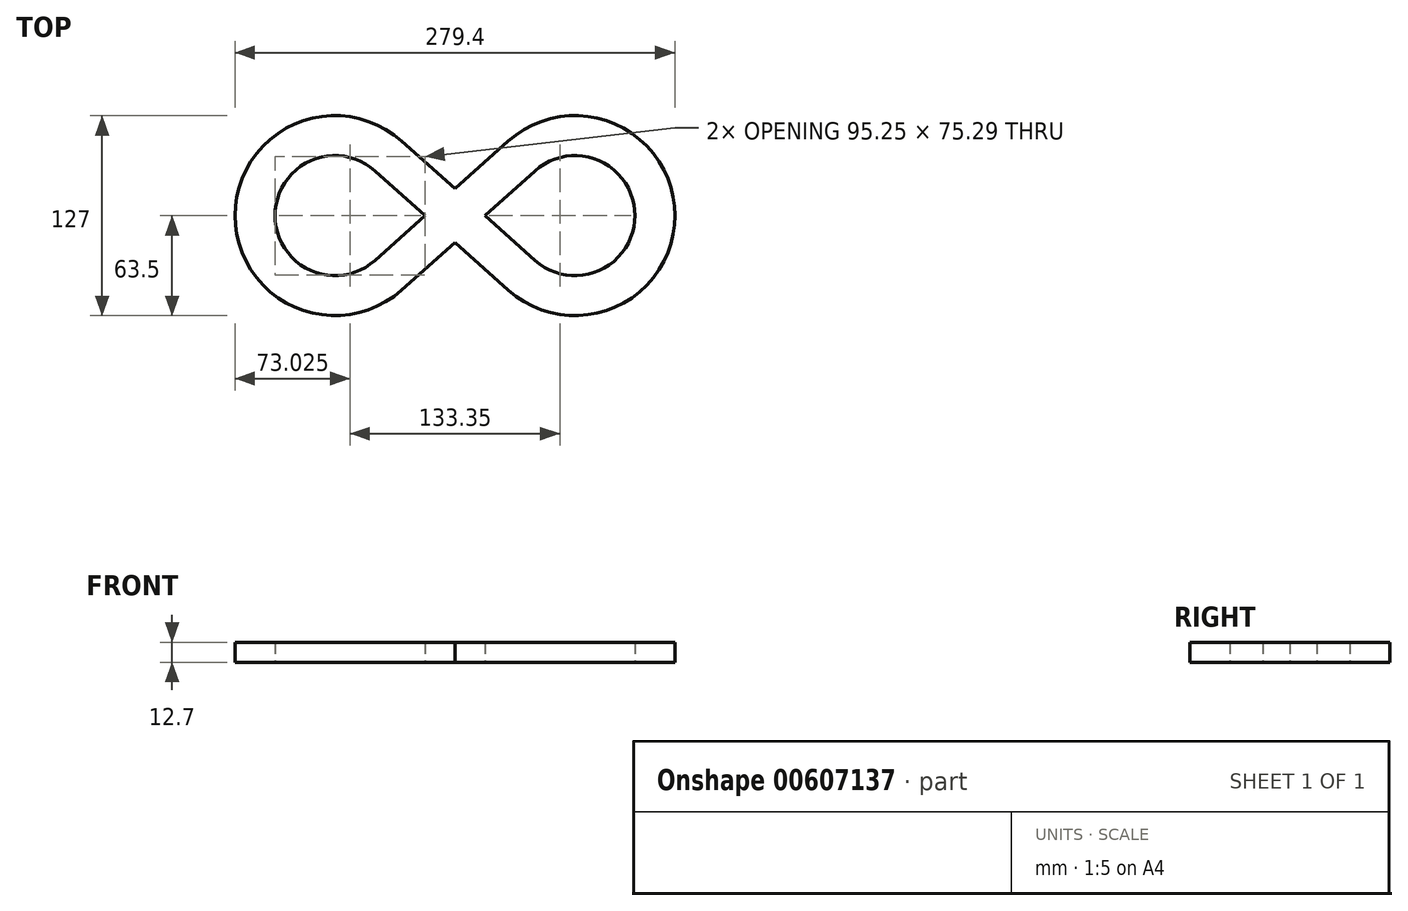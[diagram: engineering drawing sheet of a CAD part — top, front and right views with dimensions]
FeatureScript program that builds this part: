
annotation { "Feature Type Name" : "Feature", "Feature Type Description" : "" }
export const myFeature = defineFeature(function(context is Context, id is Id, definition is map)
    precondition{}
    {
        {
            var Q0;
            Q0=qCreatedBy(makeId("Top.planeOp"),FACE);
            var sketch = newSketch(context, id + "F0", { "sketchPlane" : qUnion([Q0])});
            skArc(sketch, "E0", {"start": v(-50.8, 28.4) * mm, "mid": v(-114.3, 0) * mm, "end": v(-50.8, -28.4) * mm});
            skArc(sketch, "E1", {"start": v(-33.87, 47.33) * mm, "mid": v(-139.7, 0) * mm, "end": v(-33.87, -47.33) * mm});
            skArc(sketch, "E2", {"start": v(33.87, -47.33) * mm, "mid": v(139.7, 0) * mm, "end": v(33.87, 47.33) * mm});
            skArc(sketch, "E3", {"start": v(50.8, -28.4) * mm, "mid": v(114.3, 0) * mm, "end": v(50.8, 28.4) * mm});
            skLineSegment(sketch, "E4", {"start": v(-33.87, 47.33) * mm, "end": v(50.8, -28.4) * mm});
            skLineSegment(sketch, "E5", {"start": v(-50.8, 28.4) * mm, "end": v(33.87, -47.33) * mm});
            skLineSegment(sketch, "E6", {"start": v(-50.8, -28.4) * mm, "end": v(33.87, 47.33) * mm});
            skLineSegment(sketch, "E7", {"start": v(50.8, 28.4) * mm, "end": v(-33.87, -47.33) * mm});
            skLineSegment(sketch, "E8", {"start": v(-50.8, -28.4) * mm, "end": v(-33.87, -47.33) * mm});
            skLineSegment(sketch, "E9", {"start": v(-50.8, 28.4) * mm, "end": v(-33.87, 47.33) * mm});
            skLineSegment(sketch, "E10", {"start": v(33.87, 47.33) * mm, "end": v(50.8, 28.4) * mm});
            skLineSegment(sketch, "E11", {"start": v(50.8, -28.4) * mm, "end": v(33.87, -47.33) * mm});
            skSolve(sketch);
        }
        {
            var Q0;
            {var subQ1=sQuery(id+"F0.wireOp",EDGE,"E0");Q0=makeQuery(id+"F0.imprint","IMPRINT",FACE,{"disambiguationData":[TD([[makeQuery(id+"F0.imprint","IMPRINT",EDGE,{"derivedFrom":subQ1}),-1.0]])]});}
            var Q1;
            {var subQ8=sQuery(id+"F0.wireOp",EDGE,"E2");Q1=makeQuery(id+"F0.imprint","IMPRINT",FACE,{"disambiguationData":[TD([[makeQuery(id+"F0.imprint","IMPRINT",EDGE,{"derivedFrom":subQ8}),1.0]])]});}
            var Q2;
            {var subQ0=sQuery(id+"F0.wireOp",EDGE,"E6");var subQ1=sQuery(id+"F0.wireOp",EDGE,"E4");var subQ2=makeQuery(id+"F0.imprint","INTERSECT",VERTEX,{"derivedFrom":[subQ1,subQ0]});Q2=makeQuery(id+"F0.imprint","IMPRINT",FACE,{"disambiguationData":[TD([[makeQuery(id+"F0.imprint","IMPRINT",EDGE,{"disambiguationData":[TD([[subQ2,-1.0]])],"derivedFrom":subQ1}),-1.0]])]});}
            var Q3;
            {var subQ0=sQuery(id+"F0.wireOp",EDGE,"E9");Q3=makeQuery(id+"F0.imprint","IMPRINT",FACE,{"disambiguationData":[TD([[makeQuery(id+"F0.imprint","IMPRINT",EDGE,{"derivedFrom":subQ0}),-1.0]])]});}
            var Q4;
            {var subQ5=sQuery(id+"F0.wireOp",EDGE,"E10");Q4=makeQuery(id+"F0.imprint","IMPRINT",FACE,{"disambiguationData":[TD([[makeQuery(id+"F0.imprint","IMPRINT",EDGE,{"derivedFrom":subQ5}),-1.0]])]});}
            var Q5;
            {var subQ0=sQuery(id+"F0.wireOp",EDGE,"E11");Q5=makeQuery(id+"F0.imprint","IMPRINT",FACE,{"disambiguationData":[TD([[makeQuery(id+"F0.imprint","IMPRINT",EDGE,{"derivedFrom":subQ0}),-1.0]])]});}
            var Q6;
            {var subQ5=sQuery(id+"F0.wireOp",EDGE,"E8");Q6=makeQuery(id+"F0.imprint","IMPRINT",FACE,{"disambiguationData":[TD([[makeQuery(id+"F0.imprint","IMPRINT",EDGE,{"derivedFrom":subQ5}),1.0]])]});}
            extrude(context, id + "F1", {"entities" : qUnion([Q0, Q1, Q2, Q3, Q4, Q5, Q6]), "depth" : 12.7 * mm, "offsetDistance" : 25.4 * mm});
        }
    });
